# Revit family: Haworth_Masters_Desk_ShellBowFront
name_source: partatom
category: Furniture Systems
revit_build: Autodesk Revit 2018 (Build: 20170223_1515(x64)
units: mm (PartAtom-declared; Revit-internal decimal feet)

## family parameters
Always vertical = Yes
Cut with Voids When Loaded = No
OmniClass Number = 23.40.70.14.64.21
OmniClass Title = Systems Furniture
Part Type = Normal
Room Calculation Point = No
Round Connector Dimension = Use Diameter
Shared = No
Work Plane-Based = No

## types (2) — shared parameters
Actual Depth = 36"
Actual Height = 29 1/8"
Assembly Code = E2020200
Custom Size = No
End Panel Left = Yes
End Panel Right = Yes
Manufacturer = Haworth
Max. Width = 72"
Min. Width = 66"
Model = Haworth Masters
Modesty Inset = 5 1/2"
Panel Thickness = 3/4"
Revision Number = 1
Size = Verify Final Dim. w/ Haworth
Standard Depths = 36 in.
Standard Widths = 66, 72 in.
Sustainability Info = https://www.haworth.com
URL = www.haworth.com
URL - Product = http://www.haworth.com
Warranty = http://www.haworth.com
Work Surface = Yes

## per-type parameters (varying)
| type | Actual Width | Bow Radius | Description | Width |
| 36d 66w | 66" | 93 47/64" | Haworth - Masters - Desk Bow Top Shell - 36d 66w | 66" |
| 36d 72w | 72" | 111" | Haworth - Masters - Desk Bow Top Shell - 36d 72w | 72" |

## geometry (parser evidence)
native form markers: Sweep x2
no freeform markers — native parametric forms only
